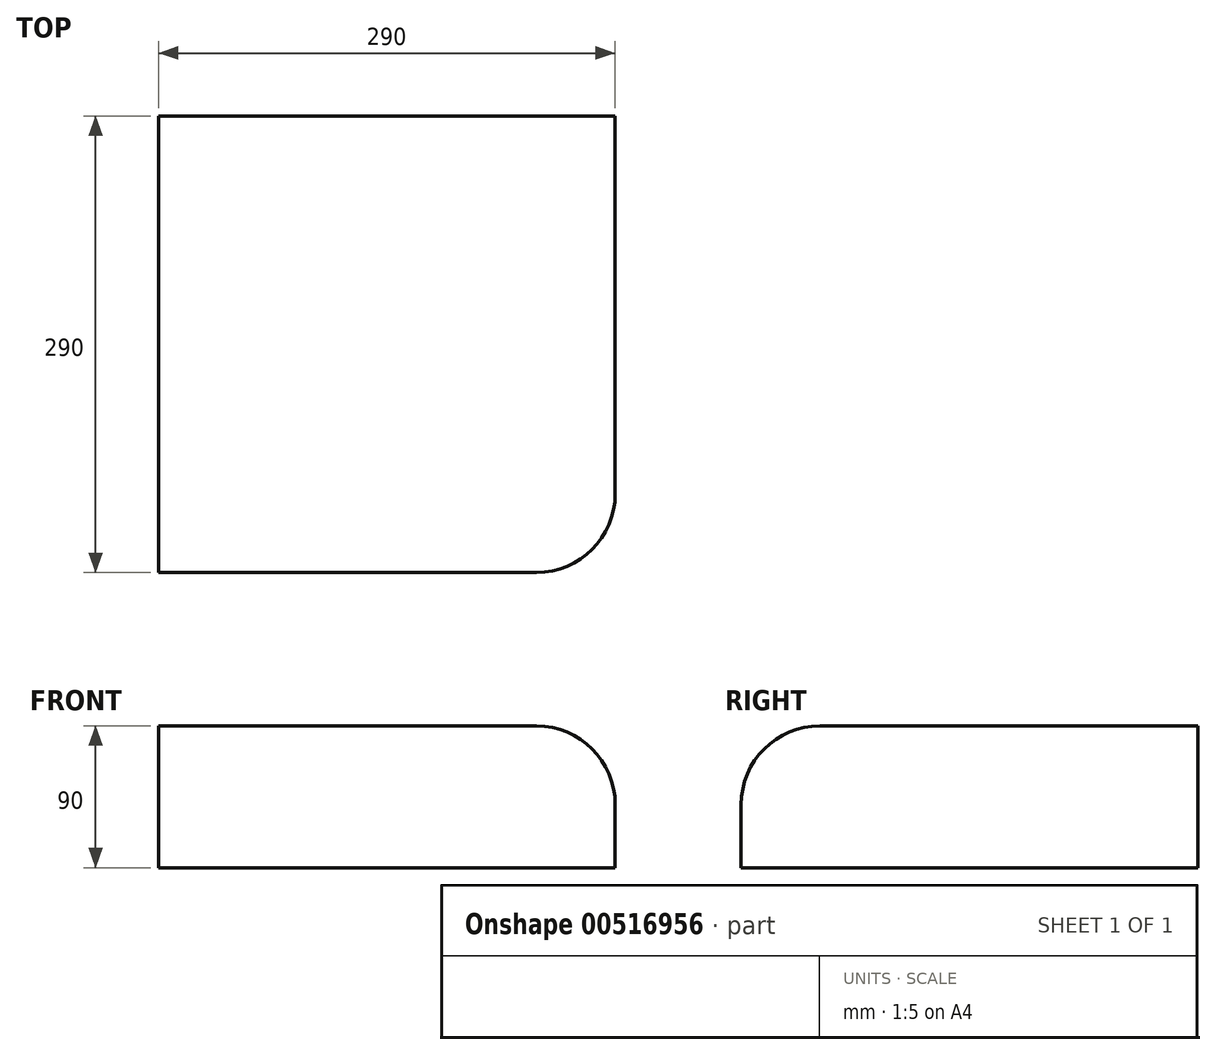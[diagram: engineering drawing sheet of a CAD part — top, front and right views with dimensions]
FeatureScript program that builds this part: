
annotation { "Feature Type Name" : "Feature", "Feature Type Description" : "" }
export const myFeature = defineFeature(function(context is Context, id is Id, definition is map)
    precondition{}
    {
        {
            var Q0;
            Q0=qCreatedBy(makeId("Top.planeOp"),FACE);
            var sketch = newSketch(context, id + "F0", { "sketchPlane" : qUnion([Q0])});
            skLineSegment(sketch, "E0.bottom", {"start": v(145, 145) * mm, "end": v(-145, 145) * mm});
            skLineSegment(sketch, "E0.top", {"start": v(145, -145) * mm, "end": v(-145, -145) * mm});
            skLineSegment(sketch, "E0.left", {"start": v(145, 145) * mm, "end": v(145, -145) * mm});
            skLineSegment(sketch, "E0.right", {"start": v(-145, 145) * mm, "end": v(-145, -145) * mm});
            skPoint(sketch, "E0.middle", {"position": v(0, 0) * mm});
            skSolve(sketch);
        }
        {
            var Q0;
            Q0 = qSketchRegion(id + "F0", true);
            extrude(context, id + "F1", {"entities" : qUnion([Q0]), "depth" : 90 * mm, "offsetDistance" : 25 * mm});
        }
        {
            var Q0;
            Q0=makeQuery(id+"F1.opExtrude","CAP_EDGE",EDGE,{"disambiguationData":[OSD([sQuery(id+"F0.wireOp",EDGE,"E0.top")])],"isStart":false});
            var Q1;
            Q1=makeQuery(id+"F1.opExtrude","SWEPT_EDGE",EDGE,{"disambiguationData":[OSD([sQuery(id+"F0.wireOp",EDGE,"E0.top"),sQuery(id+"F0.wireOp",EDGE,"E0.left")])]});
            var Q2;
            Q2=makeQuery(id+"F1.opExtrude","CAP_EDGE",EDGE,{"disambiguationData":[OSD([sQuery(id+"F0.wireOp",EDGE,"E0.left")])],"isStart":false});
            fillet(context, id + "F2", {"entities" : qUnion([Q0, Q1, Q2]), "radius" : 50 * mm, "tangentPropagation" : true, "allowEdgeOverflow" : false});
        }
    });
